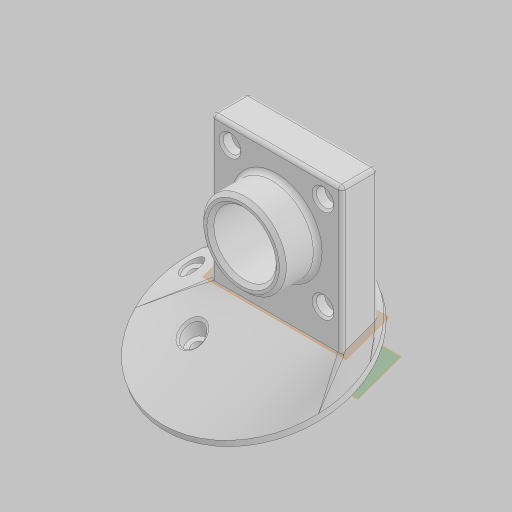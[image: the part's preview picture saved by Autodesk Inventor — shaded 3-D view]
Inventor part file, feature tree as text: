
AUTODESK INVENTOR PART (.ipt)
format: ipt  version: 2023.5 (Build 275446000, 446)  size: 467,456 bytes
history: native  units: in
note: dims shown in document units (in); Inventor stores cm internally (conversion verified against a paired STEP export)
features: extrude x7, hole x3, fillet x3, other x3, projected_geometry x3, plane x2, chamfer x2, loft x1, sketch x1, revolve x1
ambient origin geometry x8: Origin, YZ Plane, XZ Plane, XY Plane, X Axis, Y Axis, Z Axis, Center Point
bodies: Solid1 (feature_tree)
feature tree (26):
  extrude  "Extrusion1"  Depth=0.15in
  extrude  "Extrusion2"  Depth=0.15in TaperAngle=0.0deg
  plane  "Work Plane1"
  extrude  "Extrusion3"  Depth=0.15in
  loft  "Loft1"
  extrude  "Extrusion4"  Depth=0.15in
  hole  "Hole1"  [1 undecoded]
  extrude  "Extrusion5"  Depth=0.15in TaperAngle=0.0deg
  extrude  "Extrusion6"  TaperAngle=0.0deg  [1 undecoded]
  hole  "Hole2"  [1 undecoded]
  plane  "Work Plane2"
  hole  "Hole3"  [1 undecoded]
  fillet  "Fillet1"  Radius=0.3in
  chamfer  "Chamfer1"  Distance=1.1875in
  fillet  "Fillet2"  Radius=0.5in
  extrude  "Extrusion7"  Depth=0.15in
  fillet  "Fillet3"  Radius=1.3386in
  chamfer  "Chamfer2"  Distance=0.15in
  other  "Edges1"
  other  "Edges2"
  projected_geometry  "Projected Loop1"
  projected_geometry  "Projected Loop2"
  sketch  "Sketch11"  dims[d0=1.875in d1=0.525in d2=1.875in d3=0.0in d4=0.481in d5=1.875in d6=0.0in d7=0.6in d9=2.75in d10=0.1in d11=0.0in d12=0.0in d13=90.0deg d14=0.0in d15=90.0deg d16=1.6in d17=0.3in d18=0.0in d19=0.9in d20=0.75in d21=0.119in d22=0.25in d23=0.6871in d24=1.0in d25=0.8108in d26=1.1875in d27=0.5in d28=0.0in d29=0.1839in d30=1.3386in d31=0.15in d32=0.0in d33=0.094in d34=0.75in d35=0.251in d36=0.15in d37=0.6871in d38=1.0in d39=0.8108in d40=0.9792in d41=0.9792in d42=315.0deg d45=0.177in d46=0.75in d47=0.313in d48=0.45in d49=0.5635in d50=1.0in d51=0.8108in d52=0.05in d53=0.05in d54=0.125in d55=45.0deg d56=0.0625in d57=1.0in d58=1.0in d59=0.0in d60=0.25in d61=0.0312in d62=0.125in d63=45.0deg d64=0.2405in d65=90.0deg]
  other  "Srf1"
  revolve  "RevolutionSrf1"  [1 undecoded]
  projected_geometry  "Project Cut Edges1"
note: 5 required parameter values undecoded (feature->parameter linkage not recoverable at this tier; creation-order binding heuristic only, values carry confidence <= 0.55)